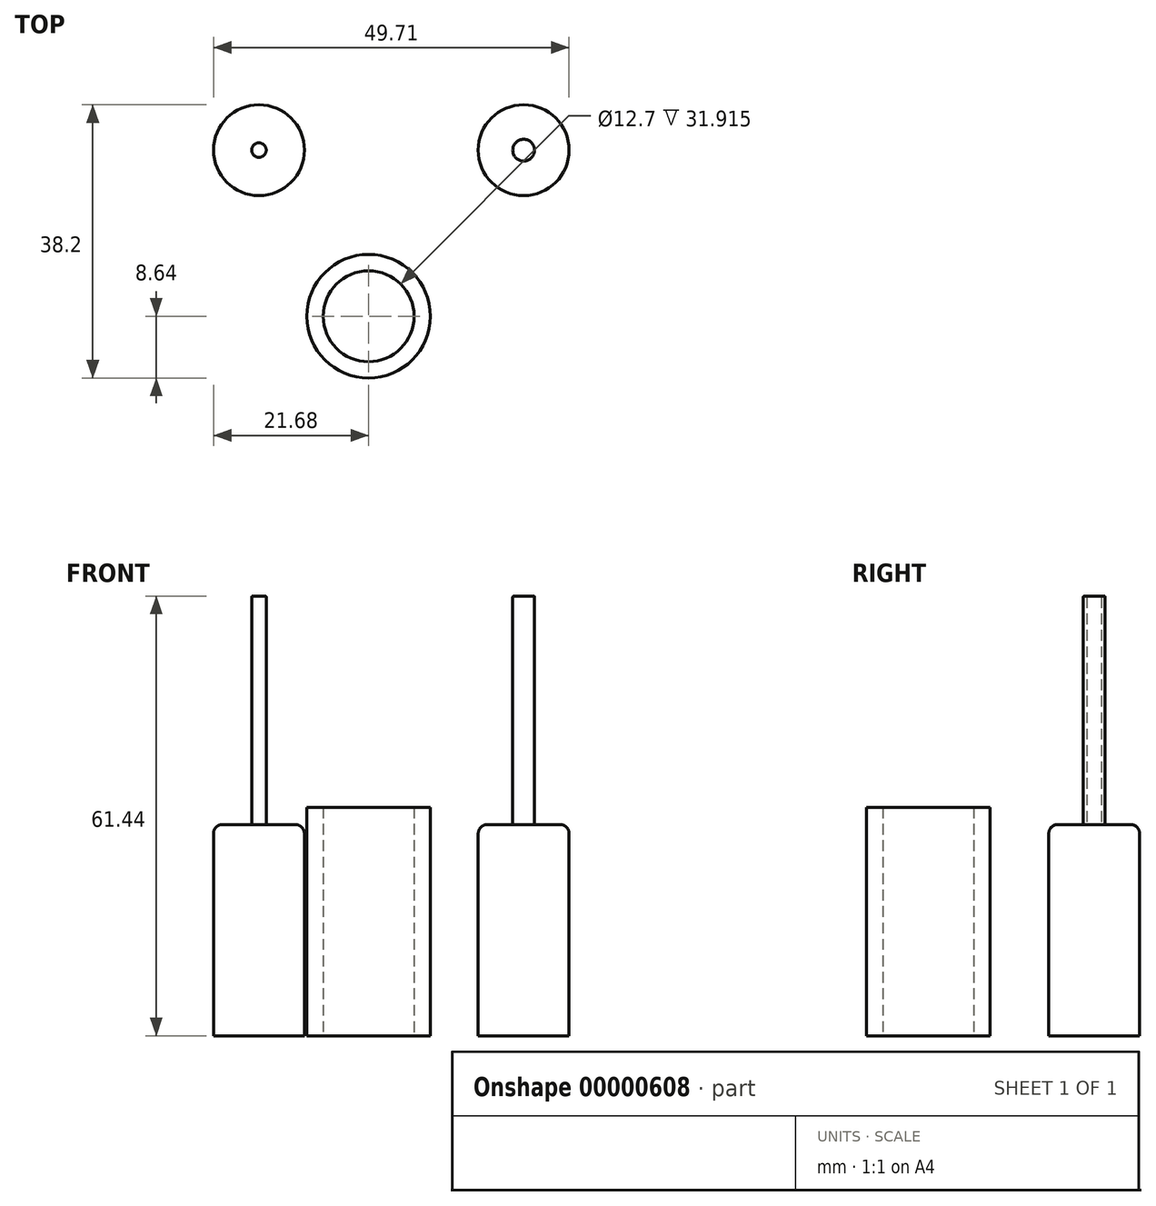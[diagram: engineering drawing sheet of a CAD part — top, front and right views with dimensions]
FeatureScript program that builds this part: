
annotation { "Feature Type Name" : "Feature", "Feature Type Description" : "" }
export const myFeature = defineFeature(function(context is Context, id is Id, definition is map)
    precondition{}
    {
        {
            var Q0;
            Q0=qCreatedBy(makeId("Top.planeOp"),FACE);
            var sketch = newSketch(context, id + "F0", { "sketchPlane" : qUnion([Q0])});
            skCircle(sketch, "E0", {"center": v(-15.33, 0) * mm, "radius": 6.35 * mm});
            skCircle(sketch, "E1", {"center": v(21.68, 0) * mm, "radius": 6.35 * mm});
            skCircle(sketch, "E2", {"center": v(0, -23.21) * mm, "radius": 6.35 * mm});
            skCircle(sketch, "E3", {"center": v(0, -23.21) * mm, "radius": 8.64 * mm});
            skSolve(sketch);
        }
        {
            var Q0;
            Q0=makeQuery(id+"F0.imprint","IMPRINT",FACE,{"disambiguationData":[TD([[makeQuery(id+"F0.imprint","IMPRINT",EDGE,{"derivedFrom":sQuery(id+"F0.wireOp",EDGE,"E0")}),1.0]])]});
            var Q1;
            Q1=makeQuery(id+"F0.imprint","IMPRINT",FACE,{"disambiguationData":[TD([[makeQuery(id+"F0.imprint","IMPRINT",EDGE,{"derivedFrom":sQuery(id+"F0.wireOp",EDGE,"E1")}),1.0]])]});
            extrude(context, id + "F1", {"entities" : qUnion([Q0, Q1]), "depth" : 29.53 * mm});
        }
        {
            var Q0;
            Q0=makeQuery(id+"F1.opExtrude","CAP_EDGE",EDGE,{"disambiguationData":[OSD([sQuery(id+"F0.wireOp",EDGE,"E1")])],"isStart":false});
            var Q1;
            Q1=makeQuery(id+"F1.opExtrude","CAP_EDGE",EDGE,{"disambiguationData":[OSD([sQuery(id+"F0.wireOp",EDGE,"E0")])],"isStart":false});
            fillet(context, id + "F2", {"entities" : qUnion([Q0, Q1]), "radius" : 1.27 * mm, "tangentPropagation" : true, "allowEdgeOverflow" : false});
        }
        {
            var Q0;
            Q0=makeQuery(id+"F1.opExtrude","CAP_FACE",FACE,{"disambiguationData":[OSD([sQuery(id+"F0.wireOp",EDGE,"E0")])],"isStart":false});
            var sketch = newSketch(context, id + "F3", { "sketchPlane" : qUnion([Q0])});
            skCircle(sketch, "E4", {"center": v(-15.33, 0) * mm, "radius": 1.02 * mm});
            skSolve(sketch);
        }
        {
            var Q0;
            Q0=makeQuery(id+"F3.imprint","IMPRINT",FACE,{"disambiguationData":[TD([[makeQuery(id+"F3.imprint","IMPRINT",EDGE,{"derivedFrom":sQuery(id+"F3.wireOp",EDGE,"E4")}),1.0]])]});
            extrude(context, id + "F4", {"entities" : qUnion([Q0]), "operationType" : NewBodyOperationType.ADD, "depth" : 31.92 * mm});
        }
        {
            var Q0;
            Q0=makeQuery(id+"F4.opExtrude","CAP_EDGE",EDGE,{"disambiguationData":[OSD([sQuery(id+"F3.wireOp",EDGE,"E4")])],"isStart":false});
            fillet(context, id + "F5", {"entities" : qUnion([Q0]), "radius" : 0.13 * mm, "tangentPropagation" : true, "allowEdgeOverflow" : false});
        }
        {
            var Q0;
            Q0=makeQuery(id+"F1.opExtrude","CAP_FACE",FACE,{"disambiguationData":[OSD([sQuery(id+"F0.wireOp",EDGE,"E1")])],"isStart":false});
            var sketch = newSketch(context, id + "F6", { "sketchPlane" : qUnion([Q0])});
            skCircle(sketch, "E5", {"center": v(21.68, 0) * mm, "radius": 1.52 * mm});
            skSolve(sketch);
        }
        {
            var Q0;
            Q0=makeQuery(id+"F6.imprint","IMPRINT",FACE,{"disambiguationData":[TD([[makeQuery(id+"F6.imprint","IMPRINT",EDGE,{"derivedFrom":sQuery(id+"F6.wireOp",EDGE,"E5")}),1.0]])]});
            extrude(context, id + "F7", {"entities" : qUnion([Q0]), "operationType" : NewBodyOperationType.ADD, "depth" : 31.92 * mm});
        }
        {
            var Q0;
            Q0=makeQuery(id+"F7.opExtrude","CAP_EDGE",EDGE,{"disambiguationData":[OSD([sQuery(id+"F6.wireOp",EDGE,"E5")])],"isStart":false});
            fillet(context, id + "F8", {"entities" : qUnion([Q0]), "radius" : 0.13 * mm, "tangentPropagation" : true, "allowEdgeOverflow" : false});
        }
        {
            var Q0;
            Q0=makeQuery(id+"F0.imprint","IMPRINT",FACE,{"disambiguationData":[TD([[makeQuery(id+"F0.imprint","IMPRINT",EDGE,{"derivedFrom":sQuery(id+"F0.wireOp",EDGE,"E2")}),-1.0]])]});
            extrude(context, id + "F9", {"entities" : qUnion([Q0]), "depth" : 31.92 * mm});
        }
    });
